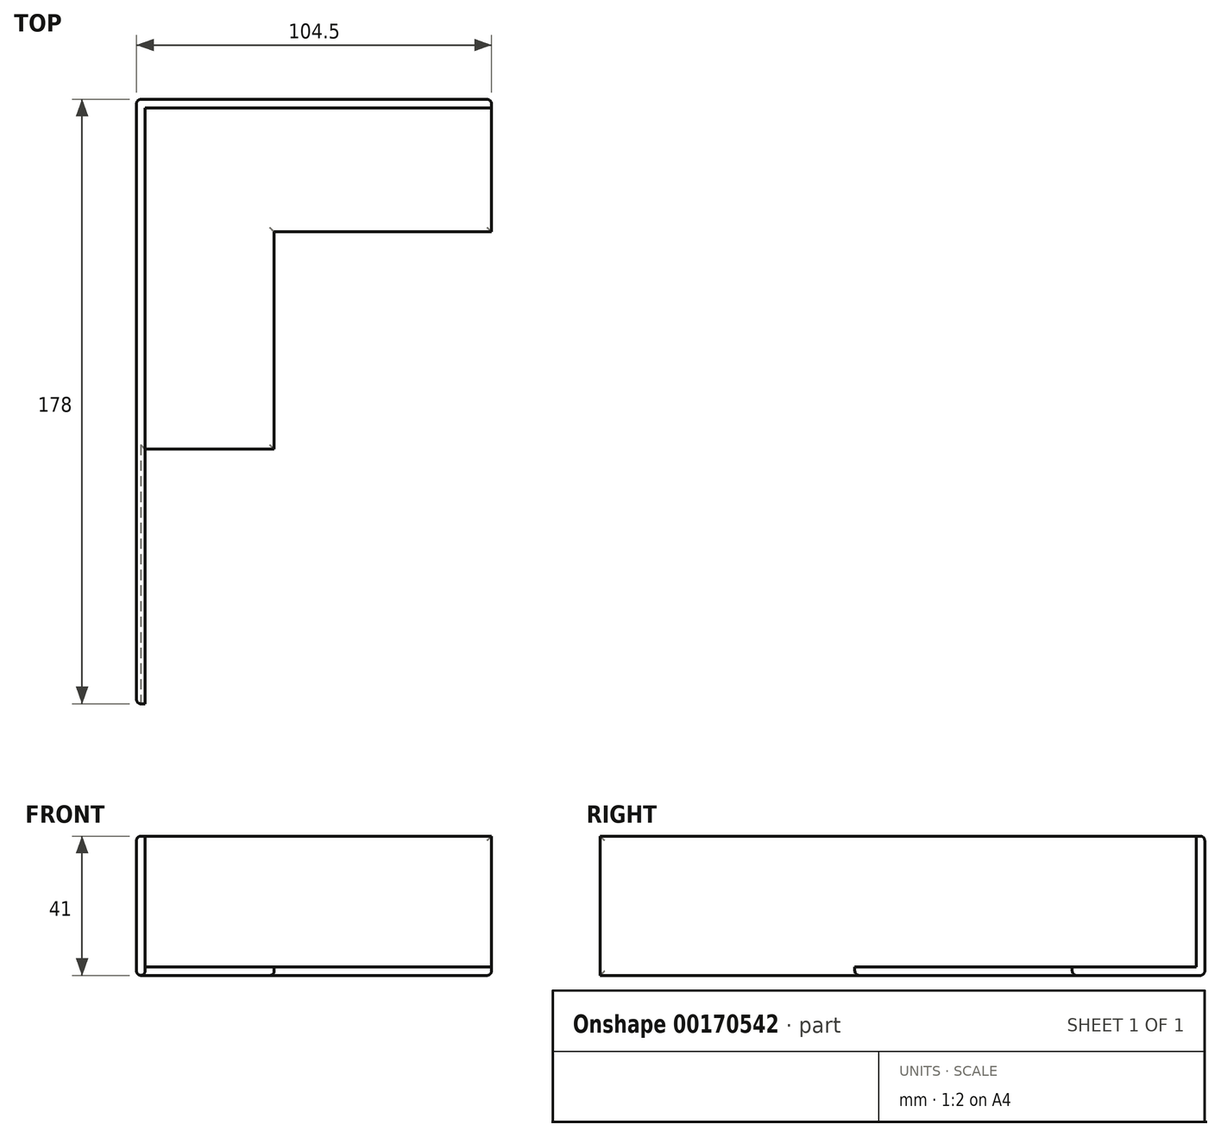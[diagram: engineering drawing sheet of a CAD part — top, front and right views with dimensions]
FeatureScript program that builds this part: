
annotation { "Feature Type Name" : "Feature", "Feature Type Description" : "" }
export const myFeature = defineFeature(function(context is Context, id is Id, definition is map)
    precondition{}
    {
        {
            var Q0;
            Q0=qCreatedBy(makeId("Top.planeOp"),FACE);
            var sketch = newSketch(context, id + "F0", { "sketchPlane" : qUnion([Q0])});
            skLineSegment(sketch, "E0", {"start": v(0, 0) * mm, "end": v(0, 102.99) * mm});
            skLineSegment(sketch, "E1", {"start": v(0, 102.99) * mm, "end": v(104.5, 102.99) * mm});
            skLineSegment(sketch, "E2", {"start": v(104.5, 102.99) * mm, "end": v(104.5, 63.99) * mm});
            skLineSegment(sketch, "E3", {"start": v(104.5, 63.99) * mm, "end": v(40.5, 63.99) * mm});
            skLineSegment(sketch, "E4", {"start": v(40.5, 63.99) * mm, "end": v(40.5, -0.01) * mm});
            skLineSegment(sketch, "E5", {"start": v(40.5, -0.01) * mm, "end": v(2.5, -0.01) * mm});
            skLineSegment(sketch, "E6", {"start": v(2.5, -0.01) * mm, "end": v(2.5, -75.01) * mm});
            skLineSegment(sketch, "E7", {"start": v(2.5, -75.01) * mm, "end": v(0, -75.01) * mm});
            skLineSegment(sketch, "E8", {"start": v(0, -75.01) * mm, "end": v(0, 102.99) * mm});
            skSolve(sketch);
        }
        {
            var Q0;
            Q0 = qSketchRegion(id + "F0", true);
            extrude(context, id + "F1", {"entities" : qUnion([Q0]), "depth" : 41 * mm});
        }
        {
            var Q0;
            Q0=makeQuery(id+"F1.opExtrude","CAP_FACE",FACE,{"disambiguationData":[OSD([sQuery(id+"F0.wireOp",EDGE,"E1"),sQuery(id+"F0.wireOp",EDGE,"E2"),sQuery(id+"F0.wireOp",EDGE,"E3"),sQuery(id+"F0.wireOp",EDGE,"E4"),sQuery(id+"F0.wireOp",EDGE,"E5"),sQuery(id+"F0.wireOp",EDGE,"E6"),sQuery(id+"F0.wireOp",EDGE,"E7"),sQuery(id+"F0.wireOp",EDGE,"E8")])],"isStart":false});
            var sketch = newSketch(context, id + "F2", { "sketchPlane" : qUnion([Q0])});
            skLineSegment(sketch, "E9", {"start": v(2.5, -0.01) * mm, "end": v(2.5, 100.49) * mm});
            skLineSegment(sketch, "E10", {"start": v(2.5, 100.49) * mm, "end": v(104.5, 100.49) * mm});
            skSolve(sketch);
        }
        {
            var Q0;
            Q0=makeQuery(id+"F2.imprint","IMPRINT",FACE,{"disambiguationData":[TD([[makeQuery(id+"F2.imprint","IMPRINT",EDGE,{"derivedFrom":sQuery(id+"F2.wireOp",EDGE,"E9")}),-1.0]])]});
            extrude(context, id + "F3", {"entities" : qUnion([Q0]), "operationType" : NewBodyOperationType.REMOVE, "oppositeDirection" : true, "depth" : 38.5 * mm});
        }
        {
            var Q0;
            Q0=makeQuery(id+"F1.opExtrude","CAP_EDGE",EDGE,{"disambiguationData":[OSD([sQuery(id+"F0.wireOp",EDGE,"E8")])],"isStart":true});
            var Q1;
            Q1=makeQuery(id+"F1.opExtrude","CAP_EDGE",EDGE,{"disambiguationData":[OSD([sQuery(id+"F0.wireOp",EDGE,"E1")])],"isStart":true});
            var Q2;
            Q2=makeQuery(id+"F1.opExtrude","CAP_EDGE",EDGE,{"disambiguationData":[OSD([sQuery(id+"F0.wireOp",EDGE,"E2")])],"isStart":true});
            var Q3;
            Q3=makeQuery(id+"F1.opExtrude","CAP_EDGE",EDGE,{"disambiguationData":[OSD([sQuery(id+"F0.wireOp",EDGE,"E3")])],"isStart":true});
            var Q4;
            Q4=makeQuery(id+"F1.opExtrude","CAP_EDGE",EDGE,{"disambiguationData":[OSD([sQuery(id+"F0.wireOp",EDGE,"E4")])],"isStart":true});
            var Q5;
            Q5=makeQuery(id+"F1.opExtrude","CAP_EDGE",EDGE,{"disambiguationData":[OSD([sQuery(id+"F0.wireOp",EDGE,"E5")])],"isStart":true});
            var Q6;
            Q6=makeQuery(id+"F1.opExtrude","CAP_EDGE",EDGE,{"disambiguationData":[OSD([sQuery(id+"F0.wireOp",EDGE,"E6")])],"isStart":true});
            fillet(context, id + "F4", {"entities" : qUnion([Q0, Q1, Q2, Q3, Q4, Q5, Q6]), "radius" : 1.27 * mm, "tangentPropagation" : true, "allowEdgeOverflow" : false});
        }
        {
            var Q0;
            Q0=makeQuery(id+"F1.opExtrude","SWEPT_EDGE",EDGE,{"disambiguationData":[OSD([sQuery(id+"F0.wireOp",EDGE,"E1"),sQuery(id+"F0.wireOp",EDGE,"E8")])]});
            var Q1;
            Q1=makeQuery(id+"F1.opExtrude","CAP_EDGE",EDGE,{"disambiguationData":[OSD([sQuery(id+"F0.wireOp",EDGE,"E8")])],"isStart":false});
            var Q2;
            Q2=makeQuery(id+"F1.opExtrude","CAP_EDGE",EDGE,{"disambiguationData":[OSD([sQuery(id+"F0.wireOp",EDGE,"E1")])],"isStart":false});
            var Q3;
            Q3=makeQuery(id+"F1.opExtrude","SWEPT_EDGE",EDGE,{"disambiguationData":[OSD([sQuery(id+"F0.wireOp",EDGE,"E7"),sQuery(id+"F0.wireOp",EDGE,"E8")])]});
            var Q4;
            Q4=makeQuery(id+"F1.opExtrude","SWEPT_EDGE",EDGE,{"disambiguationData":[OSD([sQuery(id+"F0.wireOp",EDGE,"E1"),sQuery(id+"F0.wireOp",EDGE,"E2")])]});
            fillet(context, id + "F5", {"entities" : qUnion([Q0, Q1, Q2, Q3, Q4]), "radius" : 1.27 * mm, "tangentPropagation" : true, "allowEdgeOverflow" : false});
        }
    });
